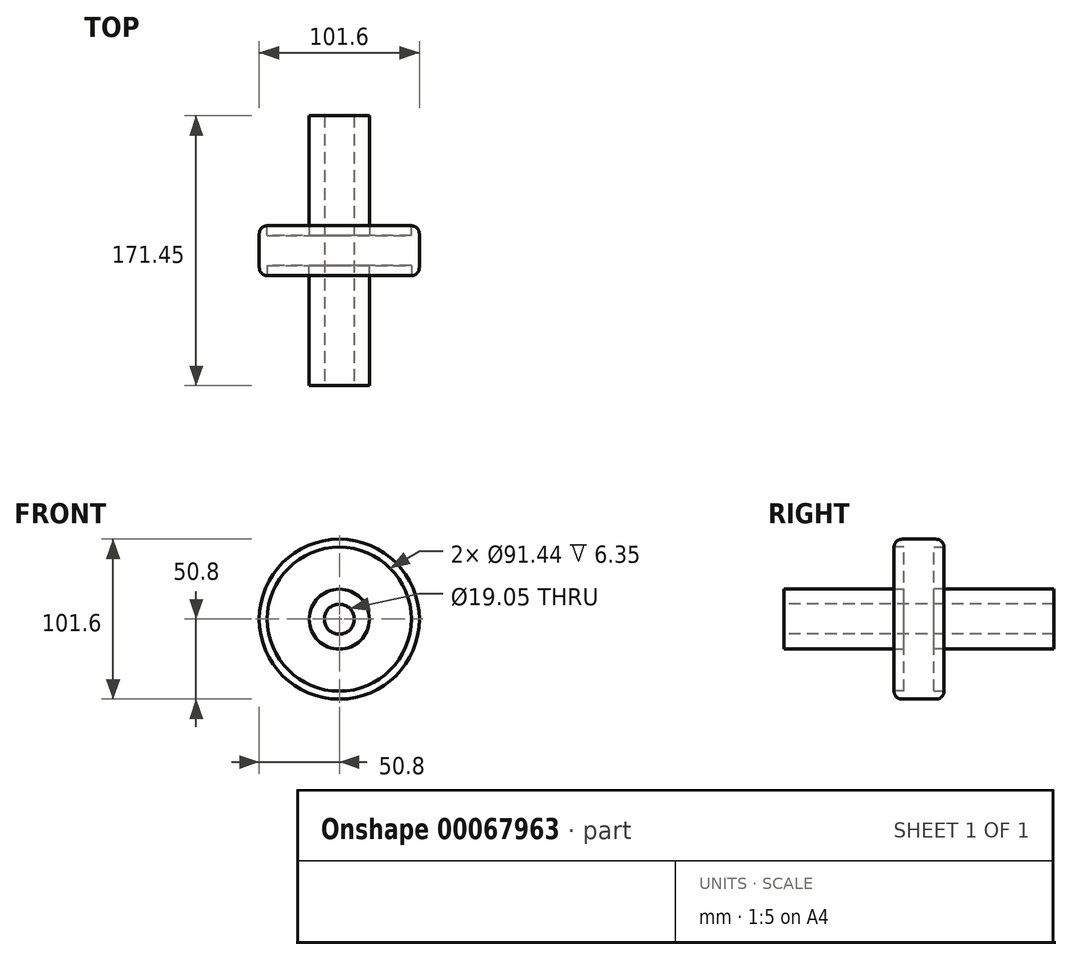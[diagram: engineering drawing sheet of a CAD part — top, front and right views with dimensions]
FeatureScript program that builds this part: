
annotation { "Feature Type Name" : "Feature", "Feature Type Description" : "" }
export const myFeature = defineFeature(function(context is Context, id is Id, definition is map)
    precondition{}
    {
        {
            var Q0;
            Q0=qCreatedBy(makeId("Front.planeOp"),FACE);
            var sketch = newSketch(context, id + "F0", { "sketchPlane" : qUnion([Q0])});
            skCircle(sketch, "E0", {"center": v(0, 0) * mm, "radius": 50.8 * mm});
            skSolve(sketch);
        }
        {
            var Q0;
            Q0=makeQuery(id+"F0.imprint","IMPRINT",FACE,{"disambiguationData":[TD([[makeQuery(id+"F0.imprint","IMPRINT",EDGE,{"derivedFrom":sQuery(id+"F0.wireOp",EDGE,"E0")}),1.0]])]});
            extrude(context, id + "F1", {"entities" : qUnion([Q0]), "depth" : 31.75 * mm});
        }
        {
            var Q0;
            Q0=makeQuery(id+"F1.opExtrude","CAP_FACE",FACE,{"disambiguationData":[OSD([sQuery(id+"F0.wireOp",EDGE,"E0")])],"isStart":false});
            var Q1;
            Q1=makeQuery(id+"F1.opExtrude","CAP_EDGE",EDGE,{"disambiguationData":[OSD([sQuery(id+"F0.wireOp",EDGE,"E0")])],"isStart":true});
            fillet(context, id + "F2", {"entities" : qUnion([Q0, Q1]), "radius" : 5.08 * mm, "tangentPropagation" : true, "allowEdgeOverflow" : false});
        }
        {
            var Q0;
            Q0=makeQuery(id+"F1.opExtrude","CAP_FACE",FACE,{"disambiguationData":[OSD([sQuery(id+"F0.wireOp",EDGE,"E0")])],"isStart":false});
            var sketch = newSketch(context, id + "F3", { "sketchPlane" : qUnion([Q0])});
            skCircle(sketch, "E1", {"center": v(0, 0) * mm, "radius": 9.53 * mm});
            skSolve(sketch);
        }
        {
            var Q0;
            Q0=makeQuery(id+"F3.imprint","IMPRINT",FACE,{"disambiguationData":[TD([[makeQuery(id+"F3.imprint","IMPRINT",EDGE,{"derivedFrom":sQuery(id+"F3.wireOp",EDGE,"E1")}),1.0]])]});
            extrude(context, id + "F4", {"entities" : qUnion([Q0]), "operationType" : NewBodyOperationType.REMOVE, "endBound" : BoundingType.THROUGH_ALL, "oppositeDirection" : true, "depth" : 25.4 * mm});
        }
        {
            var Q0;
            Q0=makeQuery(id+"F1.opExtrude","CAP_FACE",FACE,{"disambiguationData":[OSD([sQuery(id+"F0.wireOp",EDGE,"E0")])],"isStart":false});
            extrude(context, id + "F5", {"entities" : qUnion([Q0]), "operationType" : NewBodyOperationType.REMOVE, "oppositeDirection" : true, "depth" : 6.35 * mm});
        }
        {
            var Q0;
            Q0=makeQuery(id+"F1.opExtrude","CAP_FACE",FACE,{"disambiguationData":[OSD([sQuery(id+"F0.wireOp",EDGE,"E0")])],"isStart":true});
            extrude(context, id + "F6", {"entities" : qUnion([Q0]), "operationType" : NewBodyOperationType.REMOVE, "oppositeDirection" : true, "depth" : 6.35 * mm});
        }
        {
            var Q0;
            Q0=makeQuery(id+"F5.boolean.opBoolean","COPY",FACE,{"derivedFrom":makeQuery(id+"F5.opExtrude","CAP_FACE",FACE,{"disambiguationData":[OSD([sQuery(id+"F0.wireOp",EDGE,"E0")])],"isStart":false})});
            var sketch = newSketch(context, id + "F7", { "sketchPlane" : qUnion([Q0])});
            skCircle(sketch, "E2", {"center": v(0, 0) * mm, "radius": 19.05 * mm});
            skSolve(sketch);
        }
        {
            var Q0;
            Q0=makeQuery(id+"F7.imprint","IMPRINT",FACE,{"disambiguationData":[TD([[makeQuery(id+"F7.imprint","IMPRINT",EDGE,{"derivedFrom":sQuery(id+"F7.wireOp",EDGE,"E2")}),1.0]])]});
            extrude(context, id + "F8", {"entities" : qUnion([Q0]), "operationType" : NewBodyOperationType.ADD, "depth" : 76.2 * mm});
        }
        {
            var Q0;
            Q0=makeQuery(id+"F1.opExtrude","SWEPT_BODY",BODY,{"disambiguationData":[OSD([sQuery(id+"F0.wireOp",EDGE,"E0")])]});
            var Q1;
            Q1=qCreatedBy(makeId("Right.planeOp"),FACE);
            mirror(context, id + "F9", {"operationType" : NewBodyOperationType.ADD, "entities" : qUnion([Q0]), "mirrorPlane" : qUnion([Q1])});
        }
        {
            var Q0;
            Q0=makeQuery(id+"F6.boolean.opBoolean","COPY",FACE,{"derivedFrom":makeQuery(id+"F6.opExtrude","CAP_FACE",FACE,{"disambiguationData":[OSD([sQuery(id+"F0.wireOp",EDGE,"E0")])],"isStart":false})});
            var sketch = newSketch(context, id + "F10", { "sketchPlane" : qUnion([Q0])});
            skCircle(sketch, "E3", {"center": v(0, 0) * mm, "radius": 19.05 * mm});
            skSolve(sketch);
        }
        {
            var Q0;
            Q0=makeQuery(id+"F10.imprint","IMPRINT",FACE,{"disambiguationData":[TD([[makeQuery(id+"F10.imprint","IMPRINT",EDGE,{"derivedFrom":sQuery(id+"F10.wireOp",EDGE,"E3")}),1.0]])]});
            extrude(context, id + "F11", {"entities" : qUnion([Q0]), "operationType" : NewBodyOperationType.ADD, "depth" : 76.2 * mm});
        }
    });
